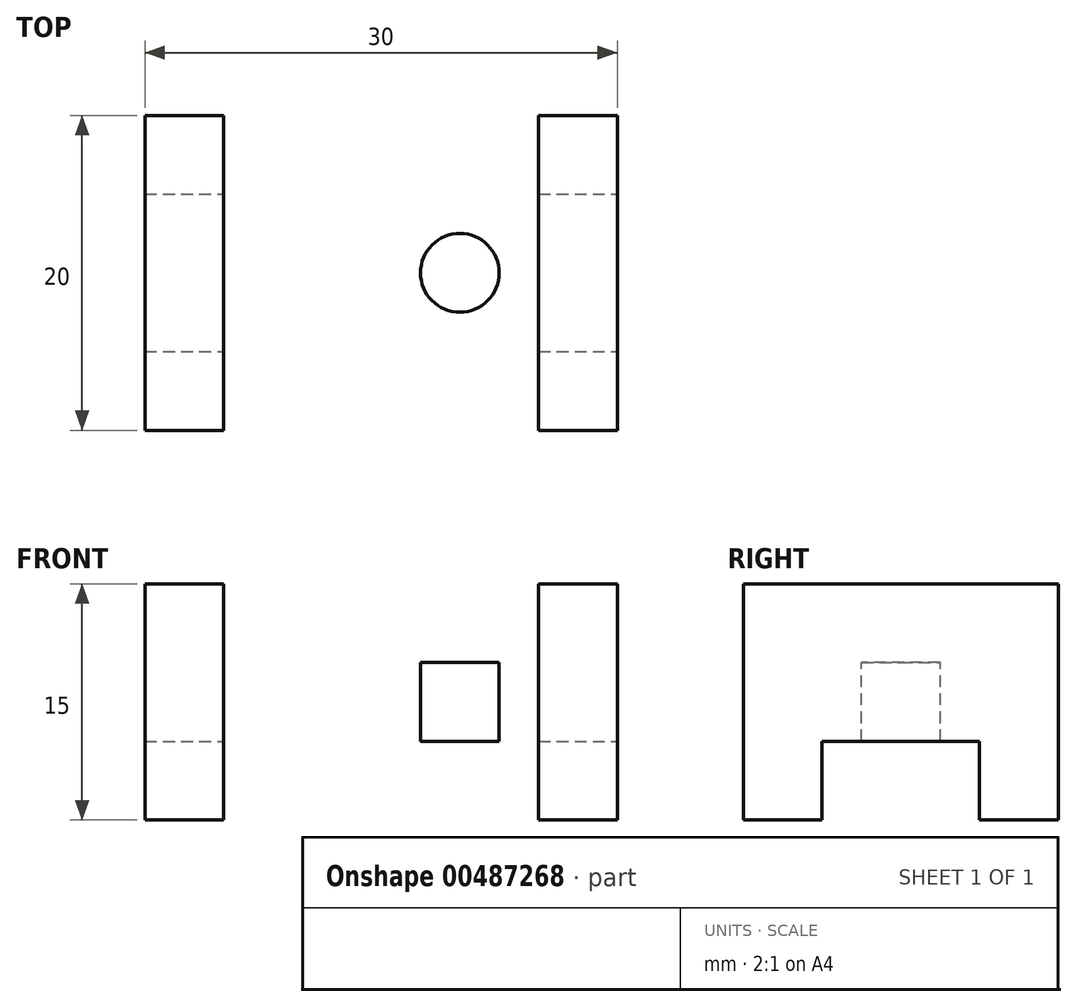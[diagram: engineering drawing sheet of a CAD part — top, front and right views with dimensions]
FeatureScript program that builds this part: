
annotation { "Feature Type Name" : "Feature", "Feature Type Description" : "" }
export const myFeature = defineFeature(function(context is Context, id is Id, definition is map)
    precondition{}
    {
        {
            var Q0;
            Q0=qCreatedBy(makeId("Top.planeOp"),FACE);
            var sketch = newSketch(context, id + "F0", { "sketchPlane" : qUnion([Q0])});
            skLineSegment(sketch, "E0.bottom", {"start": v(-10.79, -17.7) * mm, "end": v(19.21, -17.7) * mm});
            skLineSegment(sketch, "E0.top", {"start": v(-10.79, -37.7) * mm, "end": v(19.21, -37.7) * mm});
            skLineSegment(sketch, "E0.left", {"start": v(-10.79, -17.7) * mm, "end": v(-10.79, -37.7) * mm});
            skLineSegment(sketch, "E0.right", {"start": v(19.21, -17.7) * mm, "end": v(19.21, -37.7) * mm});
            skSolve(sketch);
        }
        {
            var Q0;
            Q0=makeQuery(id+"F0.imprint","IMPRINT",FACE,{"disambiguationData":[TD([[makeQuery(id+"F0.imprint","IMPRINT",EDGE,{"derivedFrom":sQuery(id+"F0.wireOp",EDGE,"E0.bottom")}),-1.0]])]});
            extrude(context, id + "F1", {"entities" : qUnion([Q0]), "depth" : 10 * mm, "offsetDistance" : 25 * mm});
        }
        {
            var Q0;
            Q0=makeQuery(id+"F1.opExtrude","CAP_FACE",FACE,{"disambiguationData":[OSD([sQuery(id+"F0.wireOp",EDGE,"E0.bottom"),sQuery(id+"F0.wireOp",EDGE,"E0.top"),sQuery(id+"F0.wireOp",EDGE,"E0.left"),sQuery(id+"F0.wireOp",EDGE,"E0.right")])],"isStart":false});
            var sketch = newSketch(context, id + "F2", { "sketchPlane" : qUnion([Q0])});
            skLineSegment(sketch, "E1", {"start": v(-10.79, -37.7) * mm, "end": v(-5.79, -37.7) * mm});
            skLineSegment(sketch, "E2", {"start": v(-5.79, -37.7) * mm, "end": v(-5.79, -17.7) * mm});
            skLineSegment(sketch, "E3", {"start": v(-5.79, -17.7) * mm, "end": v(-10.79, -17.7) * mm});
            skLineSegment(sketch, "E4", {"start": v(-10.79, -17.7) * mm, "end": v(-10.79, -37.7) * mm});
            skLineSegment(sketch, "E5", {"start": v(19.21, -37.7) * mm, "end": v(19.21, -17.7) * mm});
            skLineSegment(sketch, "E6", {"start": v(19.21, -17.7) * mm, "end": v(14.21, -17.7) * mm});
            skLineSegment(sketch, "E7", {"start": v(14.21, -17.7) * mm, "end": v(14.21, -37.7) * mm});
            skLineSegment(sketch, "E8", {"start": v(14.21, -37.7) * mm, "end": v(19.21, -37.7) * mm});
            skSolve(sketch);
        }
        {
            var Q0;
            Q0=makeQuery(id+"F2.imprint","IMPRINT",FACE,{"disambiguationData":[TD([[makeQuery(id+"F2.imprint","IMPRINT",EDGE,{"derivedFrom":sQuery(id+"F2.wireOp",EDGE,"E1")}),1.0]])]});
            var Q1;
            Q1=makeQuery(id+"F2.imprint","IMPRINT",FACE,{"disambiguationData":[TD([[makeQuery(id+"F2.imprint","IMPRINT",EDGE,{"derivedFrom":sQuery(id+"F2.wireOp",EDGE,"E5")}),-1.0]])]});
            extrude(context, id + "F3", {"entities" : qUnion([Q0, Q1]), "operationType" : NewBodyOperationType.ADD, "depth" : 5 * mm, "offsetDistance" : 25 * mm});
        }
        {
            var Q0;
            Q0=makeQuery(id+"F1.opExtrude","CAP_FACE",FACE,{"disambiguationData":[OSD([sQuery(id+"F0.wireOp",EDGE,"E0.bottom"),sQuery(id+"F0.wireOp",EDGE,"E0.top"),sQuery(id+"F0.wireOp",EDGE,"E0.left"),sQuery(id+"F0.wireOp",EDGE,"E0.right")])],"isStart":false});
            var sketch = newSketch(context, id + "F4", { "sketchPlane" : qUnion([Q0])});
            skCircle(sketch, "E9", {"center": v(-0.79, -27.7) * mm, "radius": 2.5 * mm});
            skSolve(sketch);
        }
        {
            var Q0;
            Q0 = qSketchRegion(id + "F4", true);
            extrude(context, id + "F5", {"entities" : qUnion([Q0]), "operationType" : NewBodyOperationType.REMOVE, "endBound" : BoundingType.THROUGH_ALL, "oppositeDirection" : true, "depth" : 25 * mm, "offsetDistance" : 25 * mm});
        }
        {
            var Q0;
            Q0=makeQuery(id+"F1.opExtrude","CAP_FACE",FACE,{"disambiguationData":[OSD([sQuery(id+"F0.wireOp",EDGE,"E0.bottom"),sQuery(id+"F0.wireOp",EDGE,"E0.top"),sQuery(id+"F0.wireOp",EDGE,"E0.left"),sQuery(id+"F0.wireOp",EDGE,"E0.right")])],"isStart":false});
            var sketch = newSketch(context, id + "F6", { "sketchPlane" : qUnion([Q0])});
            skLineSegment(sketch, "E10", {"start": v(14.21, -37.7) * mm, "end": v(9.21, -37.7) * mm});
            skPoint(sketch, "E11.centerSnap0", {"position": v(9.21, -27.7) * mm});
            skPoint(sketch, "E11.center.orphan", {"position": v(11.8, -27.7) * mm});
            skPoint(sketch, "E12.orphan", {"position": v(9.21, -17.7) * mm});
            skLineSegment(sketch, "E13", {"start": v(9.21, -37.7) * mm, "end": v(9.21, -17.7) * mm});
            skCircle(sketch, "E14", {"center": v(9.21, -27.7) * mm, "radius": 2.5 * mm});
            skSolve(sketch);
        }
        {
            var Q0;
            {var subQ0=sQuery(id+"F6.wireOp",EDGE,"E14");var subQ1=sQuery(id+"F6.wireOp",EDGE,"E13");var subQ2=makeQuery(id+"F6.imprint","INTERSECT",VERTEX,{"disambiguationData":[OD(0.0)],"derivedFrom":[subQ1,subQ0]});Q0=makeQuery(id+"F6.imprint","IMPRINT",FACE,{"disambiguationData":[TD([[makeQuery(id+"F6.imprint","IMPRINT",EDGE,{"disambiguationData":[TD([[subQ2,-1.0]])],"derivedFrom":subQ1}),1.0]])]});}
            var Q1;
            {var subQ0=sQuery(id+"F6.wireOp",EDGE,"E14");var subQ1=sQuery(id+"F6.wireOp",EDGE,"E13");var subQ2=makeQuery(id+"F6.imprint","INTERSECT",VERTEX,{"disambiguationData":[OD(0.0)],"derivedFrom":[subQ1,subQ0]});Q1=makeQuery(id+"F6.imprint","IMPRINT",FACE,{"disambiguationData":[TD([[makeQuery(id+"F6.imprint","IMPRINT",EDGE,{"disambiguationData":[TD([[subQ2,-1.0]])],"derivedFrom":subQ1}),-1.0]])]});}
            extrude(context, id + "F7", {"entities" : qUnion([Q0, Q1]), "operationType" : NewBodyOperationType.REMOVE, "endBound" : BoundingType.THROUGH_ALL, "oppositeDirection" : true, "depth" : 25 * mm, "offsetDistance" : 25 * mm});
        }
        {
            var Q0;
            Q0=makeQuery(id+"F3.boolean.opBoolean","MERGE",FACE,{"derivedFrom":[makeQuery(id+"F1.opExtrude","SWEPT_FACE",FACE,{"disambiguationData":[OSD([sQuery(id+"F0.wireOp",EDGE,"E0.right")])]}),makeQuery(id+"F3.opExtrude","SWEPT_FACE",FACE,{"disambiguationData":[OSD([sQuery(id+"F2.wireOp",EDGE,"E5")])]})]});
            var sketch = newSketch(context, id + "F8", { "sketchPlane" : qUnion([Q0])});
            skLineSegment(sketch, "E15", {"start": v(-37.7, 0) * mm, "end": v(-32.7, 0) * mm});
            skLineSegment(sketch, "E16", {"start": v(-17.7, 0) * mm, "end": v(-22.7, 0) * mm});
            skLineSegment(sketch, "E17", {"start": v(-32.7, 0) * mm, "end": v(-32.7, 5) * mm});
            skLineSegment(sketch, "E18", {"start": v(-32.7, 5) * mm, "end": v(-22.7, 5) * mm});
            skLineSegment(sketch, "E19", {"start": v(-22.7, 5) * mm, "end": v(-22.7, 0) * mm});
            skSolve(sketch);
        }
        {
            var Q0;
            {var subQ0=sQuery(id+"F8.wireOp",EDGE,"E17");Q0=makeQuery(id+"F8.imprint","IMPRINT",FACE,{"disambiguationData":[TD([[makeQuery(id+"F8.imprint","IMPRINT",EDGE,{"derivedFrom":subQ0}),-1.0]])]});}
            extrude(context, id + "F9", {"entities" : qUnion([Q0]), "operationType" : NewBodyOperationType.REMOVE, "endBound" : BoundingType.THROUGH_ALL, "oppositeDirection" : true, "depth" : 25 * mm, "offsetDistance" : 25 * mm});
        }
    });
